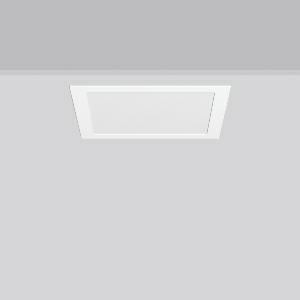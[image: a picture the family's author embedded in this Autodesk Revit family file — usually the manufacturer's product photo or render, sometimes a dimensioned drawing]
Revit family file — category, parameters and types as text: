
# Revit family: toledo_flat_square_e_672244_002_e0d8
name_source: partatom
category: Lighting Fixtures
units: mm (PartAtom-declared; Revit-internal decimal feet)

## family parameters
Cut with Voids When Loaded = No
Host = Face
Light Source = No
Part Type = Normal
Room Calculation Point = No
Round Connector Dimension = Use Diameter
Shared = No

## types (1)
- TOLEDO FLAT square E (1 x LED Modul 830, 2050 lm, 3000)
    Apparent Load = 22 VA
    CIE Flux Codes = 48 80 96 100 100
    Color Rendering = 80
    Color Temperature = 3000
    Default Elevation = 1800 mm
    Description = Series: TOLEDO FLAT square
Square recessed downlight. For escape route illumination. Housing: die-cast aluminium, powder-coated. Lightguide and diffuser made of non-yellowing plastic (PMMA). Diffuser opal matt plastic. Ceiling installation with spring system. Including separate LED converter with connecting cable 250 mm. Suitable for connection to central battery systems. External driver with simple plug-in locking system. 
Colour: white
Length: 300 mm
Width: 300 mm
Height: 3 mm
Cut-out length: 280 mm
Cut-out width: 280 mm
Recess height: 35 mm
Luminaire: recess height: 31-51 mm
Weight: 1.2 kg
Operating mode: maintained power mode
Lamp: LED
Socket: without socket
Colour temperature: 3000K
Colour rendering index (CRI): 80
System power: 22 W
Rated luminous flux: 2050 lm
Luminous flux, emergency: 2050 lm
System power, emergency: 22 W
Control gear: Regulated power supply
Protection class: II
Type of protection: IP 54
    Height = 0 mm  [stored 0 ft]
    Lamp = 1 x LED Modul 830
    Lamp Light Flux = 2050 lm
    Lamp count = 1
    Length = 300 mm
    Lifetime = 50000 h
    Luminous efficacy = 93 lm/W
    Manufacturer = RZB
    ModVariant = No
    Model = 672244.002
    Mounting Place = Ceiling
    Mounting Type = Recessed
    Number of Poles = 1
    OnlyDefault = Yes
    Power Factor = 1
    Product Name = TOLEDO FLAT square E
    Product group = Recessed downlights
    ProductGroupID = 402
    Protection Class = Protection class II
    Protection Degree = IP 40
    RLX_Detail_Level = 1
    RLX_Emergency_Light_Flux = 2050 lm
    RLX_Emergency_Type = 3
    RLX_Emergency_Type_DB = Yes
    RlxData = <blob elided: 12829 chars, md5=d090d5ce>
    Socket = socket
    Standby Power = 0 W
    System Light Flux = 2050 lm
    System Power = 22 W
    Type Comments = Product without accessories
    Type Image = 901488.002.jpg
    URL = http://relux.com
    VarID = ---
    Voltage = 230 V
    Voltage Range = 220-240 V
    Weight = 0.00 kg
    Width = 300 mm

note: [stored X ft] marks values corroborated as IEEE doubles in the binary element streams (Revit-internal decimal feet)

## geometry (parser evidence)
native form markers: Sweep x8
no freeform markers — native parametric forms only
